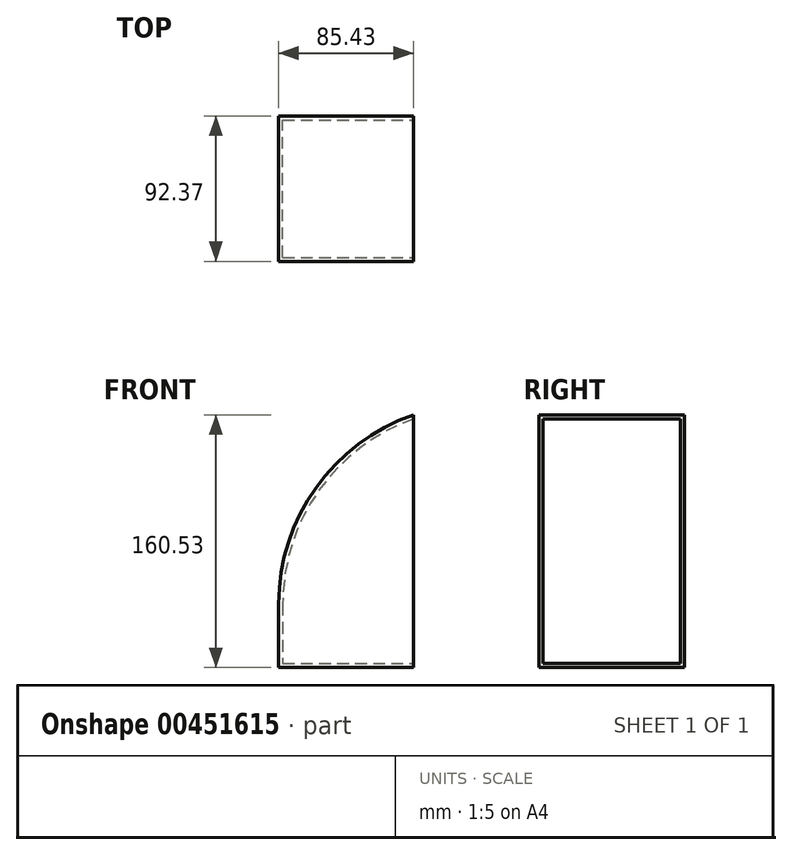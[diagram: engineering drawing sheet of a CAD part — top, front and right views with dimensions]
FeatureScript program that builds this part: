
annotation { "Feature Type Name" : "Feature", "Feature Type Description" : "" }
export const myFeature = defineFeature(function(context is Context, id is Id, definition is map)
    precondition{}
    {
        {
            var Q0;
            Q0=qCreatedBy(makeId("Top.planeOp"),FACE);
            var sketch = newSketch(context, id + "F0", { "sketchPlane" : qUnion([Q0])});
            skLineSegment(sketch, "E0.bottom", {"start": v(-168.98, -76.95) * mm, "end": v(-83.55, -76.95) * mm});
            skLineSegment(sketch, "E0.top", {"start": v(-168.98, 15.42) * mm, "end": v(-83.55, 15.42) * mm});
            skLineSegment(sketch, "E0.left", {"start": v(-168.98, -76.95) * mm, "end": v(-168.98, 15.42) * mm});
            skLineSegment(sketch, "E0.right", {"start": v(-83.55, -76.95) * mm, "end": v(-83.55, 15.42) * mm});
            skSolve(sketch);
        }
        {
            var Q0;
            Q0=makeQuery(id+"F0.imprint","IMPRINT",FACE,{"disambiguationData":[TD([[makeQuery(id+"F0.imprint","IMPRINT",EDGE,{"derivedFrom":sQuery(id+"F0.wireOp",EDGE,"E0.bottom")}),1.0]])]});
            extrude(context, id + "F1", {"entities" : qUnion([Q0]), "depth" : 160.53 * mm});
        }
        {
            var Q0;
            Q0=makeQuery(id+"F1.opExtrude","CAP_EDGE",EDGE,{"disambiguationData":[OSD([sQuery(id+"F0.wireOp",EDGE,"E0.left")])],"isStart":false});
            fillet(context, id + "F2", {"entities" : qUnion([Q0]), "radius" : 127 * mm, "tangentPropagation" : true, "allowEdgeOverflow" : false});
        }
        {
            var Q0;
            Q0=makeQuery(id+"F1.opExtrude","SWEPT_FACE",FACE,{"disambiguationData":[OSD([sQuery(id+"F0.wireOp",EDGE,"E0.right")])]});
            shell(context, id + "F3", {"entities" : qUnion([Q0]), "thickness" : 2.54 * mm});
        }
    });
